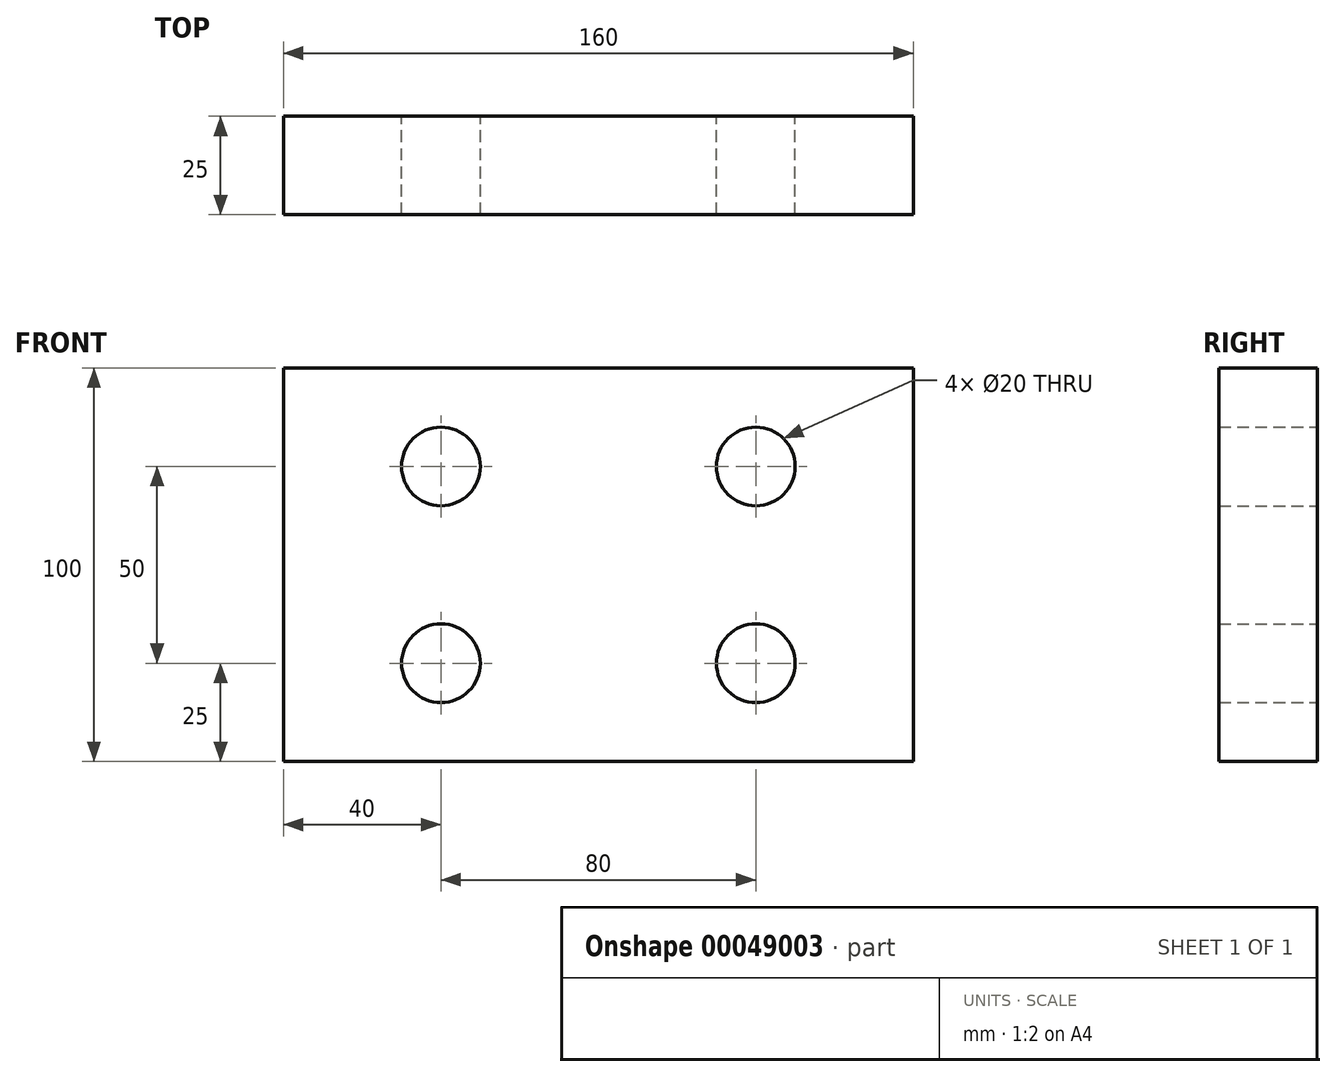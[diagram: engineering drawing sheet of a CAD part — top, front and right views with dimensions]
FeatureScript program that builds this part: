
annotation { "Feature Type Name" : "Feature", "Feature Type Description" : "" }
export const myFeature = defineFeature(function(context is Context, id is Id, definition is map)
    precondition{}
    {
        {
            var Q0;
            Q0=qCreatedBy(makeId("Front.planeOp"),FACE);
            var sketch = newSketch(context, id + "F0", { "sketchPlane" : qUnion([Q0])});
            skLineSegment(sketch, "E0.bottom", {"start": v(-80, 50) * mm, "end": v(80, 50) * mm});
            skLineSegment(sketch, "E0.top", {"start": v(-80, -50) * mm, "end": v(80, -50) * mm});
            skLineSegment(sketch, "E0.left", {"start": v(-80, 50) * mm, "end": v(-80, -50) * mm});
            skLineSegment(sketch, "E0.right", {"start": v(80, 50) * mm, "end": v(80, -50) * mm});
            skCircle(sketch, "E1", {"center": v(-40, -25) * mm, "radius": 10 * mm});
            skCircle(sketch, "E2.0.1.0", {"center": v(-40, 25) * mm, "radius": 10 * mm});
            skCircle(sketch, "E2.1.0.0", {"center": v(40, -25) * mm, "radius": 10 * mm});
            skCircle(sketch, "E2.1.1.0", {"center": v(40, 25) * mm, "radius": 10 * mm});
            skLineSegment(sketch, "E2.direction1", {"start": v(-40, -25) * mm, "end": v(40, -25) * mm, "construction": true});
            skLineSegment(sketch, "E2.direction2", {"start": v(-40, -25) * mm, "end": v(-40, 25) * mm, "construction": true});
            skSolve(sketch);
        }
        {
            var Q0;
            Q0=makeQuery(id+"F0.imprint","IMPRINT",FACE,{"disambiguationData":[TD([[makeQuery(id+"F0.imprint","IMPRINT",EDGE,{"derivedFrom":sQuery(id+"F0.wireOp",EDGE,"E0.bottom")}),-1.0]])]});
            extrude(context, id + "F1", {"entities" : qUnion([Q0]), "depth" : 25 * mm});
        }
    });
